# Revit family: Access_Door_ACUDOR_FireRated_Uninsulated_Drywall_FB-5060-DW
name_source: partatom
category: Doors
revit_build: Autodesk Revit 2017 (Build: 20171027_0315(x64)
units: mm (PartAtom-declared; Revit-internal decimal feet)

## family parameters
Cut with Voids When Loaded = No
Host = Face
Room Calculation Point = No
Shared = No

## types (7) — shared parameters
Analytic Construction = <None>
Default Elevation = 48 "
Description = FIRE RATED - FOR WALLS
Manufacturer = ACUDOR
Material Finish = Metal - Acudor - Stainless - Polished
URL = www.acudor.com
zero-valued in all types: Thickness

## per-type parameters (varying)
| type | Height | Wall Offset | Width |
| FB-5060-DW-0808 | 10.62 " | 0.5 " | 10.62 " |
| FB-5060-DW-1010 | 12.62 " | 0 " | 12.62 " |
| FB-5060-DW-1414 | 16.62 " | 0 " | 16.62 " |
| FB-5060-DW-1616 | 18.62 " | 0 " | 18.62 " |
| FB-5060-DW-1818 | 20.62 " | 0 " | 20.62 " |
| FB-5060-DW-1212 | 14.62 " | 0 " | 14.62 " |
| FB-5060-DW-2424 | 26.62 " | 0 " | 26.62 " |

note: column(s) folded — value = type name in every type: Model

## geometry (parser evidence)
native form markers: Blend x4, Sweep x13
no freeform markers — native parametric forms only
